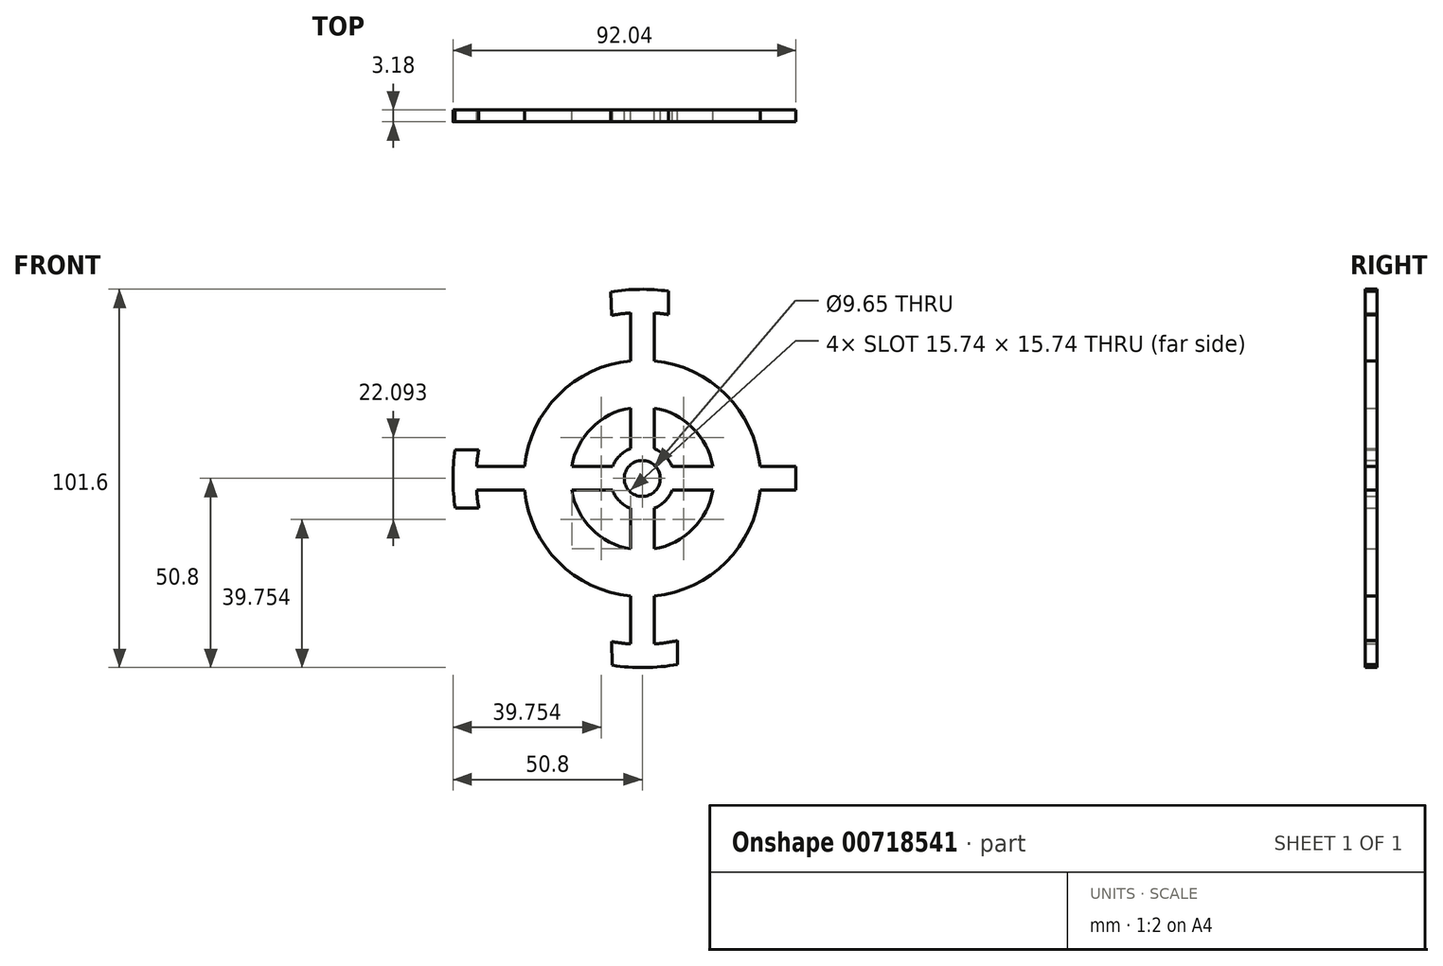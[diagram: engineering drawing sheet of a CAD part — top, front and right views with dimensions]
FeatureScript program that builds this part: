
annotation { "Feature Type Name" : "Feature", "Feature Type Description" : "" }
export const myFeature = defineFeature(function(context is Context, id is Id, definition is map)
    precondition{}
    {
        {
            var Q0;
            Q0=qCreatedBy(makeId("Front.planeOp"),FACE);
            var sketch = newSketch(context, id + "F0", { "sketchPlane" : qUnion([Q0])});
            skCircle(sketch, "E0", {"center": v(0, 0) * mm, "radius": 50.8 * mm});
            skCircle(sketch, "E1", {"center": v(0, 0) * mm, "radius": 38.1 * mm, "construction": true});
            skCircle(sketch, "E2", {"center": v(0, 0) * mm, "radius": 4.83 * mm});
            skLineSegment(sketch, "E3", {"start": v(-50.8, 0) * mm, "end": v(50.8, 0) * mm, "construction": true});
            skLineSegment(sketch, "E4", {"start": v(0, -50.8) * mm, "end": v(0, 50.8) * mm, "construction": true});
            skLineSegment(sketch, "E5", {"start": v(0, -44.45) * mm, "end": v(3.18, -44.45) * mm, "construction": true});
            skLineSegment(sketch, "E6", {"start": v(0, -44.45) * mm, "end": v(-3.18, -44.45) * mm, "construction": true});
            skLineSegment(sketch, "E7", {"start": v(0, 44.45) * mm, "end": v(-3.18, 44.45) * mm, "construction": true});
            skLineSegment(sketch, "E8", {"start": v(0, 44.45) * mm, "end": v(3.18, 44.45) * mm, "construction": true});
            skLineSegment(sketch, "E9", {"start": v(44.45, 0) * mm, "end": v(44.45, -3.18) * mm, "construction": true});
            skLineSegment(sketch, "E10", {"start": v(44.45, 0) * mm, "end": v(44.45, 3.18) * mm, "construction": true});
            skLineSegment(sketch, "E11", {"start": v(-44.45, 0) * mm, "end": v(-44.45, 3.18) * mm, "construction": true});
            skLineSegment(sketch, "E12", {"start": v(-44.45, 0) * mm, "end": v(-44.45, -3.17) * mm, "construction": true});
            skLineSegment(sketch, "E13", {"start": v(0, -8) * mm, "end": v(3.18, -8) * mm, "construction": true});
            skLineSegment(sketch, "E14", {"start": v(0, -8) * mm, "end": v(-3.18, -8) * mm, "construction": true});
            skLineSegment(sketch, "E15", {"start": v(8, 0) * mm, "end": v(8, 3.18) * mm, "construction": true});
            skLineSegment(sketch, "E16", {"start": v(8, 0) * mm, "end": v(8, -3.18) * mm, "construction": true});
            skLineSegment(sketch, "E17", {"start": v(-8, 0) * mm, "end": v(-8, 3.18) * mm, "construction": true});
            skLineSegment(sketch, "E18", {"start": v(-8, 0) * mm, "end": v(-8, -3.18) * mm, "construction": true});
            skLineSegment(sketch, "E19", {"start": v(0, 8) * mm, "end": v(3.18, 8) * mm, "construction": true});
            skLineSegment(sketch, "E20", {"start": v(0, 8) * mm, "end": v(-3.18, 8) * mm, "construction": true});
            skArc(sketch, "E21", {"start": v(3.17, 44.45) * mm, "mid": v(31.51, 31.51) * mm, "end": v(44.45, 3.17) * mm});
            skArc(sketch, "E22", {"start": v(3.18, 8) * mm, "mid": v(6.09, 6.09) * mm, "end": v(8, 3.17) * mm});
            skArc(sketch, "E23", {"start": v(-3.18, 8) * mm, "mid": v(-6.09, 6.09) * mm, "end": v(-8, 3.18) * mm});
            skArc(sketch, "E24", {"start": v(-3.18, 44.45) * mm, "mid": v(-31.51, 31.51) * mm, "end": v(-44.45, 3.18) * mm});
            skArc(sketch, "E25", {"start": v(8, -3.18) * mm, "mid": v(6.09, -6.09) * mm, "end": v(3.17, -8) * mm});
            skArc(sketch, "E26", {"start": v(44.45, -3.18) * mm, "mid": v(31.51, -31.51) * mm, "end": v(3.17, -44.45) * mm});
            skArc(sketch, "E27", {"start": v(-3.18, -8) * mm, "mid": v(-6.09, -6.09) * mm, "end": v(-8, -3.18) * mm});
            skArc(sketch, "E28", {"start": v(-3.18, -44.45) * mm, "mid": v(-31.51, -31.51) * mm, "end": v(-44.45, -3.18) * mm});
            skPoint(sketch, "E29", {"position": v(-31.62, 3.17) * mm});
            skPoint(sketch, "E30", {"position": v(-31.62, -3.17) * mm});
            skPoint(sketch, "E31", {"position": v(-3.17, 31.62) * mm});
            skPoint(sketch, "E32", {"position": v(3.17, 31.62) * mm});
            skPoint(sketch, "E33", {"position": v(31.62, 3.17) * mm});
            skPoint(sketch, "E34", {"position": v(31.62, -3.17) * mm});
            skPoint(sketch, "E35", {"position": v(3.17, -31.62) * mm});
            skPoint(sketch, "E36", {"position": v(-3.17, -31.62) * mm});
            skPoint(sketch, "E37", {"position": v(-3.18, -37.97) * mm});
            skPoint(sketch, "E38", {"position": v(3.18, -37.97) * mm});
            skPoint(sketch, "E39", {"position": v(-37.97, 3.18) * mm});
            skPoint(sketch, "E40", {"position": v(-37.97, -3.17) * mm});
            skPoint(sketch, "E41", {"position": v(37.97, 3.18) * mm});
            skPoint(sketch, "E42", {"position": v(37.97, -3.18) * mm});
            skPoint(sketch, "E43", {"position": v(3.18, 37.97) * mm});
            skPoint(sketch, "E44", {"position": v(-3.18, 37.97) * mm});
            skArc(sketch, "E45", {"start": v(-3.17, 31.62) * mm, "mid": v(-22.47, 22.47) * mm, "end": v(-31.62, 3.17) * mm});
            skArc(sketch, "E46", {"start": v(-31.62, -3.17) * mm, "mid": v(-22.47, -22.47) * mm, "end": v(-3.17, -31.62) * mm});
            skArc(sketch, "E47", {"start": v(3.18, -31.62) * mm, "mid": v(22.47, -22.47) * mm, "end": v(31.62, -3.18) * mm});
            skArc(sketch, "E48", {"start": v(3.18, 31.62) * mm, "mid": v(22.47, 22.47) * mm, "end": v(31.62, 3.18) * mm});
            skPoint(sketch, "E49", {"position": v(3.17, 18.92) * mm});
            skPoint(sketch, "E50", {"position": v(-3.17, 18.92) * mm});
            skPoint(sketch, "E51", {"position": v(-18.92, 3.17) * mm});
            skPoint(sketch, "E52", {"position": v(-18.92, -3.17) * mm});
            skPoint(sketch, "E53", {"position": v(-3.17, -18.92) * mm});
            skPoint(sketch, "E54", {"position": v(3.17, -18.92) * mm});
            skPoint(sketch, "E55", {"position": v(18.92, -3.17) * mm});
            skPoint(sketch, "E56", {"position": v(18.92, 3.17) * mm});
            skArc(sketch, "E57", {"start": v(3.17, 18.92) * mm, "mid": v(13.56, 13.56) * mm, "end": v(18.92, 3.18) * mm});
            skArc(sketch, "E58", {"start": v(18.92, -3.17) * mm, "mid": v(13.56, -13.56) * mm, "end": v(3.18, -18.92) * mm});
            skArc(sketch, "E59", {"start": v(-3.17, -18.92) * mm, "mid": v(-13.56, -13.56) * mm, "end": v(-18.92, -3.17) * mm});
            skArc(sketch, "E60", {"start": v(-18.92, 3.17) * mm, "mid": v(-13.56, 13.56) * mm, "end": v(-3.18, 18.92) * mm});
            skLineSegment(sketch, "E61", {"start": v(3.18, 8) * mm, "end": v(3.17, 18.92) * mm});
            skLineSegment(sketch, "E62", {"start": v(3.17, 31.62) * mm, "end": v(3.18, 37.97) * mm});
            skLineSegment(sketch, "E63", {"start": v(-3.18, 37.97) * mm, "end": v(-3.17, 31.62) * mm});
            skLineSegment(sketch, "E64", {"start": v(-3.17, 18.92) * mm, "end": v(-3.18, 8) * mm});
            skLineSegment(sketch, "E65", {"start": v(8, 3.18) * mm, "end": v(18.92, 3.17) * mm});
            skLineSegment(sketch, "E66", {"start": v(31.62, 3.17) * mm, "end": v(44.45, 3.18) * mm});
            skLineSegment(sketch, "E67", {"start": v(31.62, -3.17) * mm, "end": v(44.45, -3.18) * mm});
            skLineSegment(sketch, "E68", {"start": v(18.92, -3.17) * mm, "end": v(8, -3.18) * mm});
            skLineSegment(sketch, "E69", {"start": v(3.18, -8) * mm, "end": v(3.17, -18.92) * mm});
            skLineSegment(sketch, "E70", {"start": v(3.17, -31.62) * mm, "end": v(3.18, -44.45) * mm});
            skLineSegment(sketch, "E71", {"start": v(-3.18, -44.45) * mm, "end": v(-3.17, -31.62) * mm});
            skLineSegment(sketch, "E72", {"start": v(-31.62, -3.17) * mm, "end": v(-44.45, -3.18) * mm});
            skLineSegment(sketch, "E73", {"start": v(-44.45, 3.18) * mm, "end": v(-31.62, 3.17) * mm});
            skLineSegment(sketch, "E74", {"start": v(-18.92, 3.17) * mm, "end": v(-8, 3.17) * mm});
            skLineSegment(sketch, "E75", {"start": v(-8, -3.18) * mm, "end": v(-18.92, -3.17) * mm});
            skLineSegment(sketch, "E76", {"start": v(-3.18, 37.97) * mm, "end": v(-3.18, 44.45) * mm});
            skLineSegment(sketch, "E77", {"start": v(3.18, 37.97) * mm, "end": v(3.18, 44.45) * mm});
            skLineSegment(sketch, "E78", {"start": v(-3.18, -8) * mm, "end": v(-3.17, -18.92) * mm});
            skSolve(sketch);
        }
        {
            var Q0;
            Q0 = qSketchRegion(id + "F0", true);
            extrude(context, id + "F1", {"entities" : qUnion([Q0]), "depth" : 3.17 * mm, "offsetDistance" : 25.4 * mm});
        }
        {
            var Q0;
            Q0=makeQuery(id+"F1.opExtrude","CAP_FACE",FACE,{"disambiguationData":[OSD([sQuery(id+"F0.wireOp",EDGE,"E0"),sQuery(id+"F0.wireOp",EDGE,"E2"),sQuery(id+"F0.wireOp",EDGE,"E21"),sQuery(id+"F0.wireOp",EDGE,"E22"),sQuery(id+"F0.wireOp",EDGE,"E23"),sQuery(id+"F0.wireOp",EDGE,"E24"),sQuery(id+"F0.wireOp",EDGE,"E25"),sQuery(id+"F0.wireOp",EDGE,"E26"),sQuery(id+"F0.wireOp",EDGE,"E27"),sQuery(id+"F0.wireOp",EDGE,"E28"),sQuery(id+"F0.wireOp",EDGE,"E45"),sQuery(id+"F0.wireOp",EDGE,"E46"),sQuery(id+"F0.wireOp",EDGE,"E47"),sQuery(id+"F0.wireOp",EDGE,"E48"),sQuery(id+"F0.wireOp",EDGE,"E57"),sQuery(id+"F0.wireOp",EDGE,"E58"),sQuery(id+"F0.wireOp",EDGE,"E59"),sQuery(id+"F0.wireOp",EDGE,"E60"),sQuery(id+"F0.wireOp",EDGE,"E61"),sQuery(id+"F0.wireOp",EDGE,"E62"),sQuery(id+"F0.wireOp",EDGE,"E63"),sQuery(id+"F0.wireOp",EDGE,"E64"),sQuery(id+"F0.wireOp",EDGE,"E65"),sQuery(id+"F0.wireOp",EDGE,"E66"),sQuery(id+"F0.wireOp",EDGE,"E67"),sQuery(id+"F0.wireOp",EDGE,"E68"),sQuery(id+"F0.wireOp",EDGE,"E69"),sQuery(id+"F0.wireOp",EDGE,"E70"),sQuery(id+"F0.wireOp",EDGE,"E71"),sQuery(id+"F0.wireOp",EDGE,"E72"),sQuery(id+"F0.wireOp",EDGE,"E73"),sQuery(id+"F0.wireOp",EDGE,"E74"),sQuery(id+"F0.wireOp",EDGE,"E75"),sQuery(id+"F0.wireOp",EDGE,"E76"),sQuery(id+"F0.wireOp",EDGE,"E77"),sQuery(id+"F0.wireOp",EDGE,"E78")])],"isStart":false});
            var sketch = newSketch(context, id + "F2", { "sketchPlane" : qUnion([Q0])});
            skLineSegment(sketch, "E79", {"start": v(-53.39, 7.72) * mm, "end": v(-39.6, 7.72) * mm});
            skLineSegment(sketch, "E80", {"start": v(-39.6, 7.72) * mm, "end": v(-8.11, 39) * mm});
            skLineSegment(sketch, "E81", {"start": v(-8.11, 39) * mm, "end": v(-8.5, 53.2) * mm});
            skLineSegment(sketch, "E82", {"start": v(-8.5, 53.2) * mm, "end": v(-39.9, 44.5) * mm});
            skLineSegment(sketch, "E83", {"start": v(-39.9, 44.5) * mm, "end": v(-53.39, 7.72) * mm});
            skLineSegment(sketch, "E84", {"start": v(7.03, 38.48) * mm, "end": v(7.03, 55.98) * mm});
            skLineSegment(sketch, "E85", {"start": v(7.03, 55.98) * mm, "end": v(46.3, 36.35) * mm});
            skLineSegment(sketch, "E86", {"start": v(46.3, 36.35) * mm, "end": v(54.81, 8.9) * mm});
            skLineSegment(sketch, "E87", {"start": v(54.81, 8.9) * mm, "end": v(40.15, 8.9) * mm});
            skLineSegment(sketch, "E88", {"start": v(40.15, 8.9) * mm, "end": v(7.03, 38.48) * mm});
            skLineSegment(sketch, "E89", {"start": v(56.23, -6.7) * mm, "end": v(44.45, -40.05) * mm});
            skLineSegment(sketch, "E90", {"start": v(44.45, -40.05) * mm, "end": v(9.4, -54.72) * mm});
            skLineSegment(sketch, "E91", {"start": v(9.4, -54.72) * mm, "end": v(9.4, -39.34) * mm});
            skLineSegment(sketch, "E92", {"start": v(9.4, -39.34) * mm, "end": v(39.68, -6.7) * mm});
            skLineSegment(sketch, "E93", {"start": v(39.68, -6.7) * mm, "end": v(56.23, -6.7) * mm});
            skLineSegment(sketch, "E94", {"start": v(-8.3, -38.03) * mm, "end": v(-8, -54.63) * mm});
            skPoint(sketch, "E94.startSnap0", {"position": v(-3.17, -38.03) * mm});
            skLineSegment(sketch, "E95", {"start": v(-8, -54.63) * mm, "end": v(-44.45, -37.78) * mm});
            skLineSegment(sketch, "E96", {"start": v(-44.45, -37.78) * mm, "end": v(-54.22, -8) * mm});
            skLineSegment(sketch, "E97", {"start": v(-54.22, -8) * mm, "end": v(-39.7, -8) * mm});
            skLineSegment(sketch, "E98", {"start": v(-39.7, -8) * mm, "end": v(-8.3, -38.03) * mm});
            skLineSegment(sketch, "E99", {"start": v(41.24, 11.42) * mm, "end": v(41.24, -9.57) * mm});
            skLineSegment(sketch, "E100", {"start": v(41.24, -9.57) * mm, "end": v(60.48, -9.57) * mm});
            skLineSegment(sketch, "E101", {"start": v(60.48, -9.57) * mm, "end": v(60.48, 15.5) * mm});
            skLineSegment(sketch, "E102", {"start": v(60.48, 15.5) * mm, "end": v(41.24, 11.42) * mm});
            skSolve(sketch);
        }
        {
            var Q0;
            Q0 = qSketchRegion(id + "F2", true);
            extrude(context, id + "F3", {"entities" : qUnion([Q0]), "operationType" : NewBodyOperationType.REMOVE, "oppositeDirection" : true, "depth" : 25.4 * mm, "offsetDistance" : 25.4 * mm});
        }
    });
